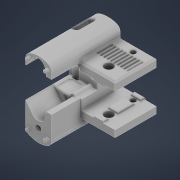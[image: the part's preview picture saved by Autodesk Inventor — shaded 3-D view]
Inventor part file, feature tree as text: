
AUTODESK INVENTOR PART (.ipt)
format: ipt  version: 2022.1 (Build 261234000, 234)  size: 1,463,296 bytes
history: native  units: mm
features: projected_geometry x35, extrude x28, sketch x28, reference x20, chamfer x18, other x11, move_body x11, direct_edit x8, fillet x7, hole x5, plane x4, delete_face x3, mirror x1
ambient origin geometry x8: Origin, YZ Plane, XZ Plane, XY Plane, X Axis, Y Axis, Z Axis, Center Point
bodies: Volumenkörper1 (feature_tree)
feature tree (179):
  extrude  "Extrusion1"  Depth=20.0mm
  extrude  "Extrusion2"  Depth=21.0mm
  plane  "Arbeitsebene1"
  extrude  "Extrusion5"  Depth=20.0mm
  sketch  "Skizze5"  dims[d7=20.0mm d8=10.0mm]
  extrude  "Extrusion6"  Depth=10.0mm
  hole  "Bohrung1"  [1 undecoded]
  extrude  "Extrusion10"  Depth=7.1mm
  sketch  "Skizze10"  dims[d28=15.0mm d29=17.0mm]
  hole  "Bohrung2"  [1 undecoded]
  hole  "Bohrung3"  [1 undecoded]
  extrude  "Extrusion11"  Depth=0.1mm
  extrude  "Extrusion12"  Depth=7.1mm
  direct_edit  "Direktbearbeitung3"
  direct_edit  "Direktbearbeitung4"
  extrude  "Extrusion13"  Depth=7.1mm
  fillet  "Rundung6"  Radius=18.2mm
  direct_edit  "Direktbearbeitung5"
  extrude  "Extrusion14"  Depth=11.0mm TaperAngle=0.0deg
  chamfer  "Fase2"  [1 undecoded]
  chamfer  "Fase3"  [1 undecoded]
  hole  "Bohrung5"  [1 undecoded]
  extrude  "Extrusion18"  Depth=4.0mm TaperAngle=0.0deg
  chamfer  "Fase4"  Distance=11.0mm
  extrude  "Extrusion19"  TaperAngle=0.0deg  [1 undecoded]
  chamfer  "Fase5"  Distance=1.2mm
  plane  "Arbeitsebene2"
  mirror  "Spiegeln1"
  extrude  "Extrusion20"  Depth=3.0mm
  fillet  "Rundung7"  Radius=1.2mm
  extrude  "Extrusion21"  Depth=3.0mm
  chamfer  "Fase6"  Distance=1.2mm
  extrude  "Extrusion22"  Depth=3.0mm
  chamfer  "Fase7"  Distance=1.2mm
  fillet  "Rundung8"  Radius=1.2mm
  chamfer  "Fase8"  Distance=6.2mm
  chamfer  "Fase9"  Distance=6.2mm
  extrude  "Extrusion23"  Depth=3.0mm
  extrude  "Extrusion24"  Depth=3.0mm
  direct_edit  "Direktbearbeitung6"
  direct_edit  "Direktbearbeitung7"
  chamfer  "Fase10"  Distance=10.561825mm
  chamfer  "Fase11"  Distance=0.8mm
  fillet  "Rundung11"  Radius=0.8mm
  sketch  "Skizze27"  dims[d66=5.2mm d67=6.0mm d68=4.0mm d69=2.0mm d70=90.0deg d71=8.0mm d72=0.0mm]
  extrude  "Extrusion25"  Depth=3.0mm
  extrude  "Extrusion26"  Depth=3.0mm
  plane  "Arbeitsebene4"
  hole  "Bohrung6"  [1 undecoded]
  chamfer  "Fase12"  Distance=0.8mm
  direct_edit  "Direktbearbeitung8"
  plane  "Arbeitsebene3"
  extrude  "Extrusion27"  Depth=3.0mm
  extrude  "Extrusion28"  Depth=3.0mm
  chamfer  "Fase14"  Distance=0.8mm
  chamfer  "Fase15"  Distance=14.53mm
  chamfer  "Fase16"  Distance=6.2385mm
  extrude  "Extrusion29"  Depth=3.0mm
  delete_face  "Fläche löschen1"
  extrude  "Extrusion30"  TaperAngle=90.0deg  [1 undecoded]
  fillet  "Rundung15"  Radius=1.0mm
  extrude  "Extrusion31"  Depth=1.0mm TaperAngle=45.0deg
  delete_face  "Fläche löschen2"
  extrude  "Extrusion32"  Depth=1.0mm TaperAngle=45.0deg
  fillet  "Rundung18"  Radius=3.95mm
  chamfer  "Fase19"  Distance=4.45mm
  chamfer  "Fase20"  Distance=7.1mm
  sketch  "Skizze36"  dims[d110=1.2mm]
  extrude  "Extrusion33"  Depth=3.0mm
  extrude  "Extrusion34"  Depth=3.0mm
  extrude  "Extrusion35"  TaperAngle=0.0deg  [1 undecoded]
  delete_face  "Fläche löschen3"
  chamfer  "Fase23"  Distance=3.55mm
  chamfer  "Fase24"  Distance=2.8mm
  direct_edit  "Direktbearbeitung11"
  direct_edit  "Direktbearbeitung12"
  extrude  "Extrusion36"  Depth=3.0mm
  fillet  "Rundung20"  Radius=2.8mm
  sketch  "Skizze1"  dims[d0=20.0mm d1=20.0mm]
  sketch  "Skizze2"  dims[d2=21.0mm d3=25.0mm]
  sketch  "Skizze4"  dims[d4=40.0mm d5=0.0mm d6=20.0mm]
  reference  "Referenz2"
  reference  "Referenz3"
  reference  "Referenz4"
  reference  "Referenz5"
  projected_geometry  "Projizierte Kontur2"
  sketch  "Skizze6"  dims[d9=0.0mm d10=0.0mm d11=-5.0mm]
  projected_geometry  "Projizierte Kontur3"
  sketch  "Skizze8"  dims[d25=7.1mm d26=7.1mm]
  reference  "Referenz6"
  reference  "Referenz7"
  projected_geometry  "Projizierte Kontur6"
  projected_geometry  "Projizierte Kontur7"
  reference  "Referenz9"
  sketch  "Skizze11"  dims[d30=1.0mm d31=18.0mm]
  projected_geometry  "Projizierte Kontur8"
  projected_geometry  "Projizierte Kontur9"
  sketch  "Skizze12"  dims[d32=18.2mm d33=0.1mm]
  projected_geometry  "Projizierte Kontur10"
  projected_geometry  "Projizierte Kontur11"
  sketch  "Skizze13"  dims[d34=36.0mm d35=0.0mm d36=7.1mm]
  projected_geometry  "Projizierte Kontur12"
  sketch  "Skizze14"  dims[d37=3.55mm d39=7.1mm d40=18.2mm]
  projected_geometry  "Projizierte Kontur13"
  projected_geometry  "Projizierte Kontur17"
  projected_geometry  "Projizierte Kontur18"
  sketch  "Skizze20"  dims[d41=9.1mm d42=11.0mm d43=0.0mm]
  projected_geometry  "Projizierte Kontur19"
  sketch  "Skizze21"  dims[d48=3.4mm d49=6.0mm d50=4.0mm d51=2.0mm d52=90.0deg d53=8.0mm d54=0.0mm d59=0.0mm d60=0.0mm]
  projected_geometry  "Projizierte Kontur20"
  sketch  "Skizze22"  dims[d61=40.0mm]
  projected_geometry  "Projizierte Kontur21"
  sketch  "Skizze23"  dims[d62=15.5mm]
  projected_geometry  "Projizierte Kontur22"
  sketch  "Skizze24"  dims[d63=10.0mm]
  projected_geometry  "Projizierte Kontur23"
  sketch  "Skizze25"  dims[d64=6.2385mm]
  reference  "Referenz12"
  reference  "Referenz13"
  reference  "Referenz14"
  reference  "Referenz15"
  sketch  "Skizze26"  dims[d65=14.53mm]
  projected_geometry  "Projizierte Kontur24"
  projected_geometry  "Projizierte Kontur25"
  projected_geometry  "Projizierte Kontur26"
  projected_geometry  "Projizierte Kontur27"
  projected_geometry  "Projizierte Kontur28"
  sketch  "Skizze28"  dims[d73=3.2mm d74=6.0mm d75=4.0mm d76=2.0mm d77=90.0deg d78=8.0mm d79=0.0mm d80=0.0mm d81=0.0mm]
  sketch  "Skizze29"  dims[d82=11.0mm d83=0.0mm d87=0.0mm d88=0.0mm d89=4.0mm]
  projected_geometry  "Projizierte Kontur29"
  sketch  "Skizze30"  dims[d90=0.0mm d91=0.0mm d92=4.0mm d93=0.0mm d94=0.0mm d95=4.0mm]
  projected_geometry  "Projizierte Kontur30"
  projected_geometry  "Projizierte Kontur31"
  reference  "Referenz18"
  sketch  "Skizze31"  dims[d101=40.0mm]
  projected_geometry  "Projizierte Kontur32"
  projected_geometry  "Projizierte Kontur33"
  projected_geometry  "Projizierte Kontur34"
  sketch  "Skizze32"  dims[d102=20.0mm d103=11.0mm d104=0.0mm]
  projected_geometry  "Projizierte Kontur35"
  sketch  "Skizze33"  dims[d105=4.0mm d106=0.0mm d107=0.0mm d108=-5.0mm]
  projected_geometry  "Projizierte Kontur36"
  projected_geometry  "Projizierte Kontur37"
  sketch  "Skizze34"  dims[d109=9.4mm]
  projected_geometry  "Projizierte Kontur38"
  projected_geometry  "Projizierte Kontur39"
  reference  "Referenz20"
  projected_geometry  "Projizierte Kontur40"
  projected_geometry  "Projizierte Kontur41"
  sketch  "Skizze37"  dims[d111=1.2mm d112=1.2mm d113=1.2mm d114=1.2mm d115=1.2mm d116=1.2mm d117=1.2mm d118=1.2mm d119=1.2mm d121=6.2mm d122=6.2mm d123=2.269mm d124=10.561825mm d125=10.561825mm d126=0.8mm d127=0.8mm d128=0.8mm d129=0.8mm d130=0.8mm d131=0.8mm d132=0.8mm d133=0.8mm d134=0.8mm d135=14.53mm d136=6.2385mm d137=8.638175mm d138=90.0deg d139=1.0mm d140=0.0mm d141=1.0mm d142=2.0mm d143=45.0deg d146=1.0mm d147=2.0mm d148=45.0deg d160=3.95mm d161=4.45mm d162=7.1mm d163=1.975mm d164=2.225mm d165=0.0mm d166=3.55mm d169=2.8mm d170=2.8mm d171=2.8mm d172=2.2mm d173=2.8mm d174=6.0mm d175=3.05mm d176=2.0mm d177=8.726646mm d178=7.2mm d179=0.0mm d180=2.0mm d181=3.6mm d182=2.0mm d183=3.6mm d184=4.95mm d185=0.0mm d186=0.5mm d187=2.0mm d188=45.0deg d189=5.8mm d190=25.0mm d191=12.5mm d192=0.0mm d193=1.0mm d194=0.0mm d195=1.0mm d196=2.0mm d197=45.0deg d198=5.0mm d199=0.0mm d200=0.0mm d201=1.0mm d202=1.0mm d203=0.0mm d204=1.0mm d205=2.0mm d206=45.0deg d207=135.0deg d208=0.0mm d209=0.0mm d210=1.0mm d211=2.0mm d212=45.0deg d213=5.0mm d214=1.0mm d215=2.0mm d216=45.0deg d217=0.7071mm d218=2.0mm d219=45.0deg d220=4.0mm d221=11.1mm d222=1.38mm d223=9.0mm d224=1.31mm d225=1.31mm d226=1.05mm d227=1.648525mm d228=1.0mm d229=0.0mm d230=0.0mm d231=6.5mm d232=0.0mm d233=0.0mm d234=0.0mm d235=1.0mm d236=0.0mm d237=0.0mm d238=6.0mm d239=0.6mm d240=2.0mm d241=45.0deg d242=0.6mm d243=2.0mm d244=45.0deg d247=0.5mm d248=0.01mm d249=0.01mm d250=0.07mm d251=0.07mm d252=0.1mm d253=0.1mm d254=10.0mm d255=0.0mm d256=10.0mm d257=0.0mm d259=3.15mm d260=6.0mm d261=6.5mm d262=3.4mm d263=90.0deg d264=20.1mm d265=0.0mm d266=0.4mm d267=2.0mm d268=45.0deg d269=0.0mm d270=0.0mm d271=0.5mm d273=7.24mm d274=5.8mm d275=0.72mm d276=6.8mm d279=1.0mm d280=5.8mm d281=2.0mm d282=19.02mm d283=0.0mm d288=5.0mm d289=0.0mm d290=0.0mm d291=1.0mm d292=2.0mm d293=45.0deg d294=1.0mm d295=2.0mm d296=45.0deg d297=3.0mm d298=2.0mm d299=45.0deg d300=9.71mm d301=0.0mm d302=0.0mm d303=0.0mm d304=1.0mm d305=2.0mm d306=0.0mm d315=2.0mm d316=2.0mm d317=2.0mm d318=0.0mm d319=0.4mm d339=0.4mm d340=2.0mm d341=45.0deg d342=0.4mm d343=2.0mm d344=45.0deg d345=8.6mm d346=0.1mm d348=0.1mm d349=0.1mm d350=0.1mm d351=0.1mm d352=24.0mm d353=12.0mm d354=4.2mm d355=0.0mm d356=0.0mm d357=10.0mm d358=0.0mm d359=1.8mm d360=10.0mm d361=0.0mm d368=0.4mm d369=2.0mm d370=45.0deg d371=0.4mm d372=2.0mm d373=45.0deg d374=0.0mm d375=0.0mm d376=-3.0mm d377=0.0mm d378=0.0mm d379=-3.0mm d380=0.0mm d381=0.0mm d382=-1.5mm d383=0.0mm d384=0.0mm d385=-2.5mm d386=4.7mm d387=3.828427mm d388=2.3mm d389=2.0mm d390=2.0mm d391=0.0mm d392=2.38mm d393=2.38mm d394=0.0mm d395=2.5mm d396=8.48mm d401=0.04mm d402=0.04mm d403=0.04mm d404=0.04mm d405=0.04mm d406=0.04mm d408=10.0mm d409=0.0mm d410=3.0mm d429=0.0mm d430=2.861mm]
  reference  "Referenz21"
  reference  "Referenz22"
  reference  "Referenz23"
  reference  "Referenz24"
  reference  "Referenz25"
  reference  "Referenz26"
  reference  "Referenz27"
  other  "<userpath>\Desktop\Voron-2-2.4r1\Custom\Front_Idlers\Baugruppe1.iam"
  other  "Baugruppe1.iam"
  other  "Inside-holder:1"
  move_body  "Verschieben3"
  move_body  "Verschieben4"
  move_body  "Verschieben5"
  move_body  "Verschieben6"
  other  "<userpath>\Desktop\Voron-2-2.4r1\CAD\VORON2_v2.4_Assembly_Step\VORON2 v2.4 Assembly.iam"
  other  "VORON2 v2.4 Assembly.iam"
  other  "Z Assembly:1"
  other  "Z Belts:1"
  other  "Z Belt:2"
  move_body  "Verschieben7"
  move_body  "Verschieben8"
  move_body  "Verschieben9"
  other  "<userpath>\Desktop\Voron-2-2.4r1\Custom\Front_Idlers\Assembly_Front-Idlers2.iam"
  other  "Assembly_Front-Idlers2.iam"
  other  "Cover1:1"
  move_body  "Verschieben16"
  move_body  "Verschieben17"
  move_body  "Verschieben18"
  move_body  "Verschieben19"
note: 10 required parameter values undecoded (feature->parameter linkage not recoverable at this tier; creation-order binding heuristic only, values carry confidence <= 0.55)
